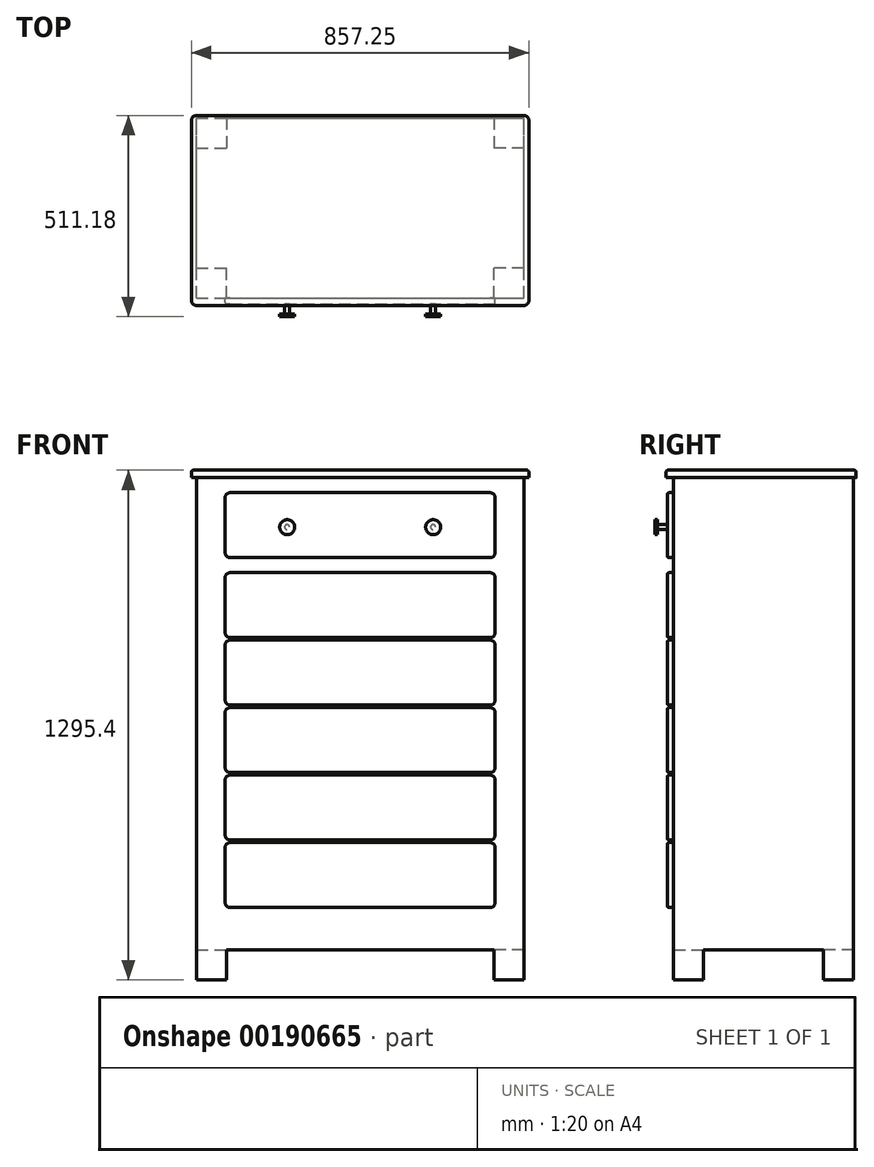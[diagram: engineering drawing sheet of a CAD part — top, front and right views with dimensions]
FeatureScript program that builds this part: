
annotation { "Feature Type Name" : "Feature", "Feature Type Description" : "" }
export const myFeature = defineFeature(function(context is Context, id is Id, definition is map)
    precondition{}
    {
        {
            var Q0;
            Q0=qCreatedBy(makeId("Top.planeOp"),FACE);
            var sketch = newSketch(context, id + "F0", { "sketchPlane" : qUnion([Q0])});
            skLineSegment(sketch, "E0.bottom", {"start": v(0, 0) * mm, "end": v(831.85, 0) * mm});
            skLineSegment(sketch, "E0.top", {"start": v(0, 457.2) * mm, "end": v(831.85, 457.2) * mm});
            skLineSegment(sketch, "E0.left", {"start": v(0, 0) * mm, "end": v(0, 457.2) * mm});
            skLineSegment(sketch, "E0.right", {"start": v(831.85, 0) * mm, "end": v(831.85, 457.2) * mm});
            skSolve(sketch);
        }
        {
            var Q0;
            Q0 = qSketchRegion(id + "F0", true);
            extrude(context, id + "F1", {"entities" : qUnion([Q0]), "depth" : 1200.15 * mm});
        }
        {
            var Q0;
            Q0=makeQuery(id+"F1.opExtrude","CAP_FACE",FACE,{"disambiguationData":[OSD([sQuery(id+"F0.wireOp",EDGE,"E0.bottom"),sQuery(id+"F0.wireOp",EDGE,"E0.top"),sQuery(id+"F0.wireOp",EDGE,"E0.left"),sQuery(id+"F0.wireOp",EDGE,"E0.right")])],"isStart":true});
            var sketch = newSketch(context, id + "F2", { "sketchPlane" : qUnion([Q0])});
            skLineSegment(sketch, "E1.bottom", {"start": v(0, 0) * mm, "end": v(76.2, 0) * mm});
            skLineSegment(sketch, "E1.top", {"start": v(0, -76.2) * mm, "end": v(76.2, -76.2) * mm});
            skLineSegment(sketch, "E1.left", {"start": v(0, 0) * mm, "end": v(0, -76.2) * mm});
            skLineSegment(sketch, "E1.right", {"start": v(76.2, 0) * mm, "end": v(76.2, -76.2) * mm});
            skLineSegment(sketch, "E2.bottom", {"start": v(0, -457.2) * mm, "end": v(76.2, -457.2) * mm});
            skLineSegment(sketch, "E2.top", {"start": v(0, -381) * mm, "end": v(76.2, -381) * mm});
            skLineSegment(sketch, "E2.left", {"start": v(0, -457.2) * mm, "end": v(0, -381) * mm});
            skLineSegment(sketch, "E2.right", {"start": v(76.2, -457.2) * mm, "end": v(76.2, -381) * mm});
            skLineSegment(sketch, "E3.bottom", {"start": v(831.85, 0) * mm, "end": v(755.65, 0) * mm});
            skLineSegment(sketch, "E3.top", {"start": v(831.85, -76.2) * mm, "end": v(755.65, -76.2) * mm});
            skLineSegment(sketch, "E3.left", {"start": v(831.85, 0) * mm, "end": v(831.85, -76.2) * mm});
            skLineSegment(sketch, "E3.right", {"start": v(755.65, 0) * mm, "end": v(755.65, -76.2) * mm});
            skLineSegment(sketch, "E4.bottom", {"start": v(831.85, -457.2) * mm, "end": v(755.65, -457.2) * mm});
            skLineSegment(sketch, "E4.top", {"start": v(831.85, -381) * mm, "end": v(755.65, -381) * mm});
            skLineSegment(sketch, "E4.left", {"start": v(831.85, -457.2) * mm, "end": v(831.85, -381) * mm});
            skLineSegment(sketch, "E4.right", {"start": v(755.65, -457.2) * mm, "end": v(755.65, -381) * mm});
            skSolve(sketch);
        }
        {
            var Q0;
            Q0 = qSketchRegion(id + "F2", true);
            extrude(context, id + "F3", {"entities" : qUnion([Q0]), "operationType" : NewBodyOperationType.ADD, "depth" : 76.2 * mm});
        }
        {
            var Q0;
            Q0=makeQuery(id+"F1.opExtrude","CAP_FACE",FACE,{"disambiguationData":[OSD([sQuery(id+"F0.wireOp",EDGE,"E0.bottom"),sQuery(id+"F0.wireOp",EDGE,"E0.top"),sQuery(id+"F0.wireOp",EDGE,"E0.left"),sQuery(id+"F0.wireOp",EDGE,"E0.right")])],"isStart":false});
            var sketch = newSketch(context, id + "F4", { "sketchPlane" : qUnion([Q0])});
            skLineSegment(sketch, "E5.bottom", {"start": v(0, 463.55) * mm, "end": v(831.85, 463.55) * mm});
            skLineSegment(sketch, "E5.top", {"start": v(0, -19.05) * mm, "end": v(831.85, -19.05) * mm});
            skLineSegment(sketch, "E5.left", {"start": v(-12.7, 450.85) * mm, "end": v(-12.7, -6.35) * mm});
            skLineSegment(sketch, "E5.right", {"start": v(844.55, 450.85) * mm, "end": v(844.55, -6.35) * mm});
            skPoint(sketch, "E6.visualSharp", {"position": v(-12.7, 463.55) * mm});
            skArc(sketch, "E6.filletArc", {"start": v(0, 463.55) * mm, "mid": v(-8.98, 459.83) * mm, "end": v(-12.7, 450.85) * mm});
            skPoint(sketch, "E7.visualSharp", {"position": v(-12.7, -19.05) * mm});
            skArc(sketch, "E7.filletArc", {"start": v(-12.7, -6.35) * mm, "mid": v(-8.98, -15.33) * mm, "end": v(0, -19.05) * mm});
            skPoint(sketch, "E8.visualSharp", {"position": v(844.55, 463.55) * mm});
            skArc(sketch, "E8.filletArc", {"start": v(844.55, 450.85) * mm, "mid": v(840.83, 459.83) * mm, "end": v(831.85, 463.55) * mm});
            skPoint(sketch, "E9.visualSharp", {"position": v(844.55, -19.05) * mm});
            skArc(sketch, "E9.filletArc", {"start": v(831.85, -19.05) * mm, "mid": v(840.83, -15.33) * mm, "end": v(844.55, -6.35) * mm});
            skSolve(sketch);
        }
        {
            var Q0;
            Q0 = qSketchRegion(id + "F4", true);
            extrude(context, id + "F5", {"entities" : qUnion([Q0]), "operationType" : NewBodyOperationType.ADD, "depth" : 19.05 * mm});
        }
        {
            var Q0;
            Q0=makeQuery(id+"F3.boolean.opBoolean","MERGE",FACE,{"derivedFrom":[makeQuery(id+"F1.opExtrude","SWEPT_FACE",FACE,{"disambiguationData":[OSD([sQuery(id+"F0.wireOp",EDGE,"E0.bottom")])]}),makeQuery(id+"F3.opExtrude","SWEPT_FACE",FACE,{"disambiguationData":[OSD([sQuery(id+"F2.wireOp",EDGE,"E1.bottom")])]}),makeQuery(id+"F3.opExtrude","SWEPT_FACE",FACE,{"disambiguationData":[OSD([sQuery(id+"F2.wireOp",EDGE,"E3.bottom")])]})]});
            var sketch = newSketch(context, id + "F6", { "sketchPlane" : qUnion([Q0])});
            skLineSegment(sketch, "E10.bottom", {"start": v(85.72, 1162.05) * mm, "end": v(746.13, 1162.05) * mm});
            skLineSegment(sketch, "E10.top", {"start": v(85.72, 996.95) * mm, "end": v(746.13, 996.95) * mm});
            skLineSegment(sketch, "E10.left", {"start": v(73.03, 1149.35) * mm, "end": v(73.03, 1009.65) * mm});
            skLineSegment(sketch, "E10.right", {"start": v(758.83, 1149.35) * mm, "end": v(758.83, 1009.65) * mm});
            skLineSegment(sketch, "E11", {"start": v(73.03, 1162.05) * mm, "end": v(0, 1162.05) * mm, "construction": true});
            skLineSegment(sketch, "E12", {"start": v(758.83, 1162.05) * mm, "end": v(831.85, 1162.05) * mm, "construction": true});
            skPoint(sketch, "E13.visualSharp", {"position": v(73.03, 1162.05) * mm});
            skArc(sketch, "E13.filletArc", {"start": v(85.72, 1162.05) * mm, "mid": v(76.74, 1158.33) * mm, "end": v(73.03, 1149.35) * mm});
            skPoint(sketch, "E14.visualSharp", {"position": v(73.03, 996.95) * mm});
            skArc(sketch, "E14.filletArc", {"start": v(73.03, 1009.65) * mm, "mid": v(76.74, 1000.67) * mm, "end": v(85.72, 996.95) * mm});
            skPoint(sketch, "E15.visualSharp", {"position": v(758.83, 996.95) * mm});
            skArc(sketch, "E15.filletArc", {"start": v(746.13, 996.95) * mm, "mid": v(755.1, 1000.67) * mm, "end": v(758.83, 1009.65) * mm});
            skPoint(sketch, "E16.visualSharp", {"position": v(758.83, 1162.05) * mm});
            skArc(sketch, "E16.filletArc", {"start": v(758.83, 1149.35) * mm, "mid": v(755.1, 1158.33) * mm, "end": v(746.13, 1162.05) * mm});
            skLineSegment(sketch, "E17.bottom", {"start": v(85.72, 958.85) * mm, "end": v(746.12, 958.85) * mm});
            skLineSegment(sketch, "E17.top", {"start": v(85.72, 793.75) * mm, "end": v(746.12, 793.75) * mm});
            skLineSegment(sketch, "E17.left", {"start": v(73.02, 946.15) * mm, "end": v(73.02, 806.45) * mm});
            skLineSegment(sketch, "E17.right", {"start": v(758.83, 946.15) * mm, "end": v(758.83, 806.45) * mm});
            skLineSegment(sketch, "E18", {"start": v(73.02, 958.85) * mm, "end": v(0, 958.85) * mm, "construction": true});
            skLineSegment(sketch, "E19", {"start": v(758.83, 958.85) * mm, "end": v(831.85, 958.85) * mm, "construction": true});
            skPoint(sketch, "E20.visualSharp", {"position": v(73.02, 958.85) * mm});
            skArc(sketch, "E20.filletArc", {"start": v(85.72, 958.85) * mm, "mid": v(76.74, 955.13) * mm, "end": v(73.03, 946.15) * mm});
            skPoint(sketch, "E21.visualSharp", {"position": v(73.02, 793.75) * mm});
            skArc(sketch, "E21.filletArc", {"start": v(73.03, 806.45) * mm, "mid": v(76.74, 797.47) * mm, "end": v(85.72, 793.75) * mm});
            skPoint(sketch, "E22.visualSharp", {"position": v(758.83, 793.75) * mm});
            skArc(sketch, "E22.filletArc", {"start": v(746.12, 793.75) * mm, "mid": v(755.1, 797.47) * mm, "end": v(758.82, 806.45) * mm});
            skPoint(sketch, "E23.visualSharp", {"position": v(758.83, 958.85) * mm});
            skArc(sketch, "E23.filletArc", {"start": v(758.82, 946.15) * mm, "mid": v(755.1, 955.13) * mm, "end": v(746.12, 958.85) * mm});
            skLineSegment(sketch, "E24.bottom", {"start": v(85.73, 787.4) * mm, "end": v(746.12, 787.4) * mm});
            skLineSegment(sketch, "E24.top", {"start": v(85.73, 622.3) * mm, "end": v(746.12, 622.3) * mm});
            skLineSegment(sketch, "E24.left", {"start": v(73.03, 774.7) * mm, "end": v(73.03, 635) * mm});
            skLineSegment(sketch, "E24.right", {"start": v(758.83, 774.7) * mm, "end": v(758.83, 635) * mm});
            skLineSegment(sketch, "E25", {"start": v(73.03, 787.4) * mm, "end": v(0, 787.4) * mm, "construction": true});
            skLineSegment(sketch, "E26", {"start": v(758.83, 787.4) * mm, "end": v(831.85, 787.4) * mm, "construction": true});
            skPoint(sketch, "E27.visualSharp", {"position": v(73.03, 787.4) * mm});
            skArc(sketch, "E27.filletArc", {"start": v(85.73, 787.4) * mm, "mid": v(76.74, 783.68) * mm, "end": v(73.03, 774.7) * mm});
            skPoint(sketch, "E28.visualSharp", {"position": v(73.03, 622.3) * mm});
            skArc(sketch, "E28.filletArc", {"start": v(73.03, 635) * mm, "mid": v(76.74, 626.02) * mm, "end": v(85.73, 622.3) * mm});
            skPoint(sketch, "E29.visualSharp", {"position": v(758.83, 622.3) * mm});
            skArc(sketch, "E29.filletArc", {"start": v(746.12, 622.3) * mm, "mid": v(755.1, 626.02) * mm, "end": v(758.82, 635) * mm});
            skPoint(sketch, "E30.visualSharp", {"position": v(758.83, 787.4) * mm});
            skArc(sketch, "E30.filletArc", {"start": v(758.82, 774.7) * mm, "mid": v(755.1, 783.68) * mm, "end": v(746.12, 787.4) * mm});
            skLineSegment(sketch, "E31.bottom", {"start": v(85.73, 615.95) * mm, "end": v(746.12, 615.95) * mm});
            skLineSegment(sketch, "E31.top", {"start": v(85.73, 450.85) * mm, "end": v(746.12, 450.85) * mm});
            skLineSegment(sketch, "E31.left", {"start": v(73.03, 603.25) * mm, "end": v(73.03, 463.55) * mm});
            skLineSegment(sketch, "E31.right", {"start": v(758.83, 603.25) * mm, "end": v(758.83, 463.55) * mm});
            skLineSegment(sketch, "E32", {"start": v(73.03, 615.95) * mm, "end": v(0, 615.95) * mm, "construction": true});
            skLineSegment(sketch, "E33", {"start": v(758.83, 615.95) * mm, "end": v(831.85, 615.95) * mm, "construction": true});
            skPoint(sketch, "E34.visualSharp", {"position": v(73.03, 615.95) * mm});
            skArc(sketch, "E34.filletArc", {"start": v(85.73, 615.95) * mm, "mid": v(76.74, 612.23) * mm, "end": v(73.03, 603.25) * mm});
            skPoint(sketch, "E35.visualSharp", {"position": v(73.03, 450.85) * mm});
            skArc(sketch, "E35.filletArc", {"start": v(73.03, 463.55) * mm, "mid": v(76.74, 454.57) * mm, "end": v(85.73, 450.85) * mm});
            skPoint(sketch, "E36.visualSharp", {"position": v(758.83, 450.85) * mm});
            skArc(sketch, "E36.filletArc", {"start": v(746.12, 450.85) * mm, "mid": v(755.1, 454.57) * mm, "end": v(758.82, 463.55) * mm});
            skPoint(sketch, "E37.visualSharp", {"position": v(758.83, 615.95) * mm});
            skArc(sketch, "E37.filletArc", {"start": v(758.82, 603.25) * mm, "mid": v(755.1, 612.23) * mm, "end": v(746.12, 615.95) * mm});
            skLineSegment(sketch, "E38.bottom", {"start": v(85.72, 444.5) * mm, "end": v(746.12, 444.5) * mm});
            skLineSegment(sketch, "E38.top", {"start": v(85.72, 279.4) * mm, "end": v(746.12, 279.4) * mm});
            skLineSegment(sketch, "E38.left", {"start": v(73.02, 431.8) * mm, "end": v(73.02, 292.1) * mm});
            skLineSegment(sketch, "E38.right", {"start": v(758.83, 431.8) * mm, "end": v(758.83, 292.1) * mm});
            skLineSegment(sketch, "E39", {"start": v(73.02, 444.5) * mm, "end": v(0, 444.5) * mm, "construction": true});
            skLineSegment(sketch, "E40", {"start": v(758.83, 444.5) * mm, "end": v(831.85, 444.5) * mm, "construction": true});
            skPoint(sketch, "E41.visualSharp", {"position": v(73.02, 444.5) * mm});
            skArc(sketch, "E41.filletArc", {"start": v(85.72, 444.5) * mm, "mid": v(76.74, 440.78) * mm, "end": v(73.03, 431.8) * mm});
            skPoint(sketch, "E42.visualSharp", {"position": v(73.02, 279.4) * mm});
            skArc(sketch, "E42.filletArc", {"start": v(73.03, 292.1) * mm, "mid": v(76.74, 283.12) * mm, "end": v(85.72, 279.4) * mm});
            skPoint(sketch, "E43.visualSharp", {"position": v(758.83, 279.4) * mm});
            skArc(sketch, "E43.filletArc", {"start": v(746.12, 279.4) * mm, "mid": v(755.1, 283.12) * mm, "end": v(758.82, 292.1) * mm});
            skPoint(sketch, "E44.visualSharp", {"position": v(758.83, 444.5) * mm});
            skArc(sketch, "E44.filletArc", {"start": v(758.82, 431.8) * mm, "mid": v(755.1, 440.78) * mm, "end": v(746.12, 444.5) * mm});
            skLineSegment(sketch, "E45.bottom", {"start": v(85.73, 273.05) * mm, "end": v(746.12, 273.05) * mm});
            skLineSegment(sketch, "E45.top", {"start": v(85.73, 107.95) * mm, "end": v(746.12, 107.95) * mm});
            skLineSegment(sketch, "E45.left", {"start": v(73.03, 260.35) * mm, "end": v(73.03, 120.65) * mm});
            skLineSegment(sketch, "E45.right", {"start": v(758.83, 260.35) * mm, "end": v(758.83, 120.65) * mm});
            skLineSegment(sketch, "E46", {"start": v(73.03, 273.05) * mm, "end": v(0, 273.05) * mm, "construction": true});
            skLineSegment(sketch, "E47", {"start": v(758.83, 273.05) * mm, "end": v(831.85, 273.05) * mm, "construction": true});
            skPoint(sketch, "E48.visualSharp", {"position": v(73.03, 273.05) * mm});
            skArc(sketch, "E48.filletArc", {"start": v(85.73, 273.05) * mm, "mid": v(76.74, 269.33) * mm, "end": v(73.03, 260.35) * mm});
            skPoint(sketch, "E49.visualSharp", {"position": v(73.03, 107.95) * mm});
            skArc(sketch, "E49.filletArc", {"start": v(73.03, 120.65) * mm, "mid": v(76.74, 111.67) * mm, "end": v(85.73, 107.95) * mm});
            skPoint(sketch, "E50.visualSharp", {"position": v(758.83, 107.95) * mm});
            skArc(sketch, "E50.filletArc", {"start": v(746.12, 107.95) * mm, "mid": v(755.1, 111.67) * mm, "end": v(758.82, 120.65) * mm});
            skPoint(sketch, "E51.visualSharp", {"position": v(758.83, 273.05) * mm});
            skArc(sketch, "E51.filletArc", {"start": v(758.82, 260.35) * mm, "mid": v(755.1, 269.33) * mm, "end": v(746.12, 273.05) * mm});
            skSolve(sketch);
        }
        {
            var Q0;
            Q0 = qSketchRegion(id + "F6", true);
            extrude(context, id + "F7", {"entities" : qUnion([Q0]), "operationType" : NewBodyOperationType.ADD, "depth" : 15.88 * mm});
        }
        {
            var Q0;
            Q0=makeQuery(id+"F7.opExtrude","CAP_FACE",FACE,{"disambiguationData":[OSD([sQuery(id+"F6.wireOp",EDGE,"E10.bottom"),sQuery(id+"F6.wireOp",EDGE,"E10.top"),sQuery(id+"F6.wireOp",EDGE,"E10.left"),sQuery(id+"F6.wireOp",EDGE,"E10.right"),sQuery(id+"F6.wireOp",EDGE,"E13.filletArc"),sQuery(id+"F6.wireOp",EDGE,"E14.filletArc"),sQuery(id+"F6.wireOp",EDGE,"E15.filletArc"),sQuery(id+"F6.wireOp",EDGE,"E16.filletArc")])],"isStart":false});
            var Q1;
            Q1=makeQuery(id+"F7.opExtrude","CAP_FACE",FACE,{"disambiguationData":[OSD([sQuery(id+"F6.wireOp",EDGE,"E17.bottom"),sQuery(id+"F6.wireOp",EDGE,"E17.top"),sQuery(id+"F6.wireOp",EDGE,"E17.left"),sQuery(id+"F6.wireOp",EDGE,"E17.right"),sQuery(id+"F6.wireOp",EDGE,"E20.filletArc"),sQuery(id+"F6.wireOp",EDGE,"E21.filletArc"),sQuery(id+"F6.wireOp",EDGE,"E22.filletArc"),sQuery(id+"F6.wireOp",EDGE,"E23.filletArc")])],"isStart":false});
            var Q2;
            Q2=makeQuery(id+"F7.opExtrude","CAP_FACE",FACE,{"disambiguationData":[OSD([sQuery(id+"F6.wireOp",EDGE,"E24.bottom"),sQuery(id+"F6.wireOp",EDGE,"E24.top"),sQuery(id+"F6.wireOp",EDGE,"E24.left"),sQuery(id+"F6.wireOp",EDGE,"E24.right"),sQuery(id+"F6.wireOp",EDGE,"E27.filletArc"),sQuery(id+"F6.wireOp",EDGE,"E28.filletArc"),sQuery(id+"F6.wireOp",EDGE,"E29.filletArc"),sQuery(id+"F6.wireOp",EDGE,"E30.filletArc")])],"isStart":false});
            var Q3;
            Q3=makeQuery(id+"F7.opExtrude","CAP_FACE",FACE,{"disambiguationData":[OSD([sQuery(id+"F6.wireOp",EDGE,"E31.bottom"),sQuery(id+"F6.wireOp",EDGE,"E31.top"),sQuery(id+"F6.wireOp",EDGE,"E31.left"),sQuery(id+"F6.wireOp",EDGE,"E31.right"),sQuery(id+"F6.wireOp",EDGE,"E34.filletArc"),sQuery(id+"F6.wireOp",EDGE,"E35.filletArc"),sQuery(id+"F6.wireOp",EDGE,"E36.filletArc"),sQuery(id+"F6.wireOp",EDGE,"E37.filletArc")])],"isStart":false});
            var Q4;
            Q4=makeQuery(id+"F7.opExtrude","CAP_FACE",FACE,{"disambiguationData":[OSD([sQuery(id+"F6.wireOp",EDGE,"E38.bottom"),sQuery(id+"F6.wireOp",EDGE,"E38.top"),sQuery(id+"F6.wireOp",EDGE,"E38.left"),sQuery(id+"F6.wireOp",EDGE,"E38.right"),sQuery(id+"F6.wireOp",EDGE,"E41.filletArc"),sQuery(id+"F6.wireOp",EDGE,"E42.filletArc"),sQuery(id+"F6.wireOp",EDGE,"E43.filletArc"),sQuery(id+"F6.wireOp",EDGE,"E44.filletArc")])],"isStart":false});
            var Q5;
            Q5=makeQuery(id+"F7.opExtrude","CAP_FACE",FACE,{"disambiguationData":[OSD([sQuery(id+"F6.wireOp",EDGE,"E45.bottom"),sQuery(id+"F6.wireOp",EDGE,"E45.top"),sQuery(id+"F6.wireOp",EDGE,"E45.left"),sQuery(id+"F6.wireOp",EDGE,"E45.right"),sQuery(id+"F6.wireOp",EDGE,"E48.filletArc"),sQuery(id+"F6.wireOp",EDGE,"E49.filletArc"),sQuery(id+"F6.wireOp",EDGE,"E50.filletArc"),sQuery(id+"F6.wireOp",EDGE,"E51.filletArc")])],"isStart":false});
            fillet(context, id + "F8", {"entities" : qUnion([Q0, Q1, Q2, Q3, Q4, Q5]), "radius" : 5.08 * mm, "tangentPropagation" : true, "allowEdgeOverflow" : false});
        }
        {
            var Q0;
            Q0=makeQuery(id+"F7.opExtrude","CAP_FACE",FACE,{"disambiguationData":[OSD([sQuery(id+"F6.wireOp",EDGE,"E10.bottom"),sQuery(id+"F6.wireOp",EDGE,"E10.top"),sQuery(id+"F6.wireOp",EDGE,"E10.left"),sQuery(id+"F6.wireOp",EDGE,"E10.right"),sQuery(id+"F6.wireOp",EDGE,"E13.filletArc"),sQuery(id+"F6.wireOp",EDGE,"E14.filletArc"),sQuery(id+"F6.wireOp",EDGE,"E15.filletArc"),sQuery(id+"F6.wireOp",EDGE,"E16.filletArc")])],"isStart":false});
            var sketch = newSketch(context, id + "F9", { "sketchPlane" : qUnion([Q0])});
            skCircle(sketch, "E52", {"center": v(230.5, 1074.42) * mm, "radius": 6.35 * mm});
            skLineSegment(sketch, "E53", {"start": v(415.93, 1156.97) * mm, "end": v(415.93, 1002.03) * mm, "construction": true});
            skCircle(sketch, "E54.MirrorC", {"center": v(601.35, 1074.42) * mm, "radius": 6.35 * mm});
            skSolve(sketch);
        }
        {
            var Q0;
            Q0 = qSketchRegion(id + "F9", true);
            extrude(context, id + "F10", {"entities" : qUnion([Q0]), "operationType" : NewBodyOperationType.ADD, "depth" : 25.4 * mm});
        }
        {
            var Q0;
            Q0=makeQuery(id+"F10.opExtrude","CAP_FACE",FACE,{"disambiguationData":[OSD([sQuery(id+"F9.wireOp",EDGE,"E52")])],"isStart":false});
            var sketch = newSketch(context, id + "F11", { "sketchPlane" : qUnion([Q0])});
            skCircle(sketch, "E55", {"center": v(230.5, 1074.42) * mm, "radius": 19.05 * mm});
            skSolve(sketch);
        }
        {
            var Q0;
            Q0 = qSketchRegion(id + "F11", true);
            extrude(context, id + "F12", {"entities" : qUnion([Q0]), "operationType" : NewBodyOperationType.ADD, "depth" : 6.35 * mm});
        }
        {
            var Q0;
            Q0=makeQuery(id+"F10.opExtrude","CAP_FACE",FACE,{"disambiguationData":[OSD([sQuery(id+"F9.wireOp",EDGE,"E54.MirrorC")])],"isStart":false});
            var sketch = newSketch(context, id + "F13", { "sketchPlane" : qUnion([Q0])});
            skCircle(sketch, "E56", {"center": v(601.35, 1074.42) * mm, "radius": 19.05 * mm});
            skSolve(sketch);
        }
        {
            var Q0;
            Q0 = qSketchRegion(id + "F13", true);
            extrude(context, id + "F14", {"entities" : qUnion([Q0]), "operationType" : NewBodyOperationType.ADD, "depth" : 6.35 * mm});
        }
        {
            var Q0;
            Q0=makeQuery(id+"F5.opExtrude","CAP_FACE",FACE,{"disambiguationData":[OSD([sQuery(id+"F4.wireOp",EDGE,"E5.bottom"),sQuery(id+"F4.wireOp",EDGE,"E5.top"),sQuery(id+"F4.wireOp",EDGE,"E5.left"),sQuery(id+"F4.wireOp",EDGE,"E5.right"),sQuery(id+"F4.wireOp",EDGE,"E6.filletArc"),sQuery(id+"F4.wireOp",EDGE,"E7.filletArc"),sQuery(id+"F4.wireOp",EDGE,"E8.filletArc"),sQuery(id+"F4.wireOp",EDGE,"E9.filletArc")])],"isStart":false});
            fillet(context, id + "F15", {"entities" : qUnion([Q0]), "radius" : 5.08 * mm, "tangentPropagation" : true, "allowEdgeOverflow" : false});
        }
    });
